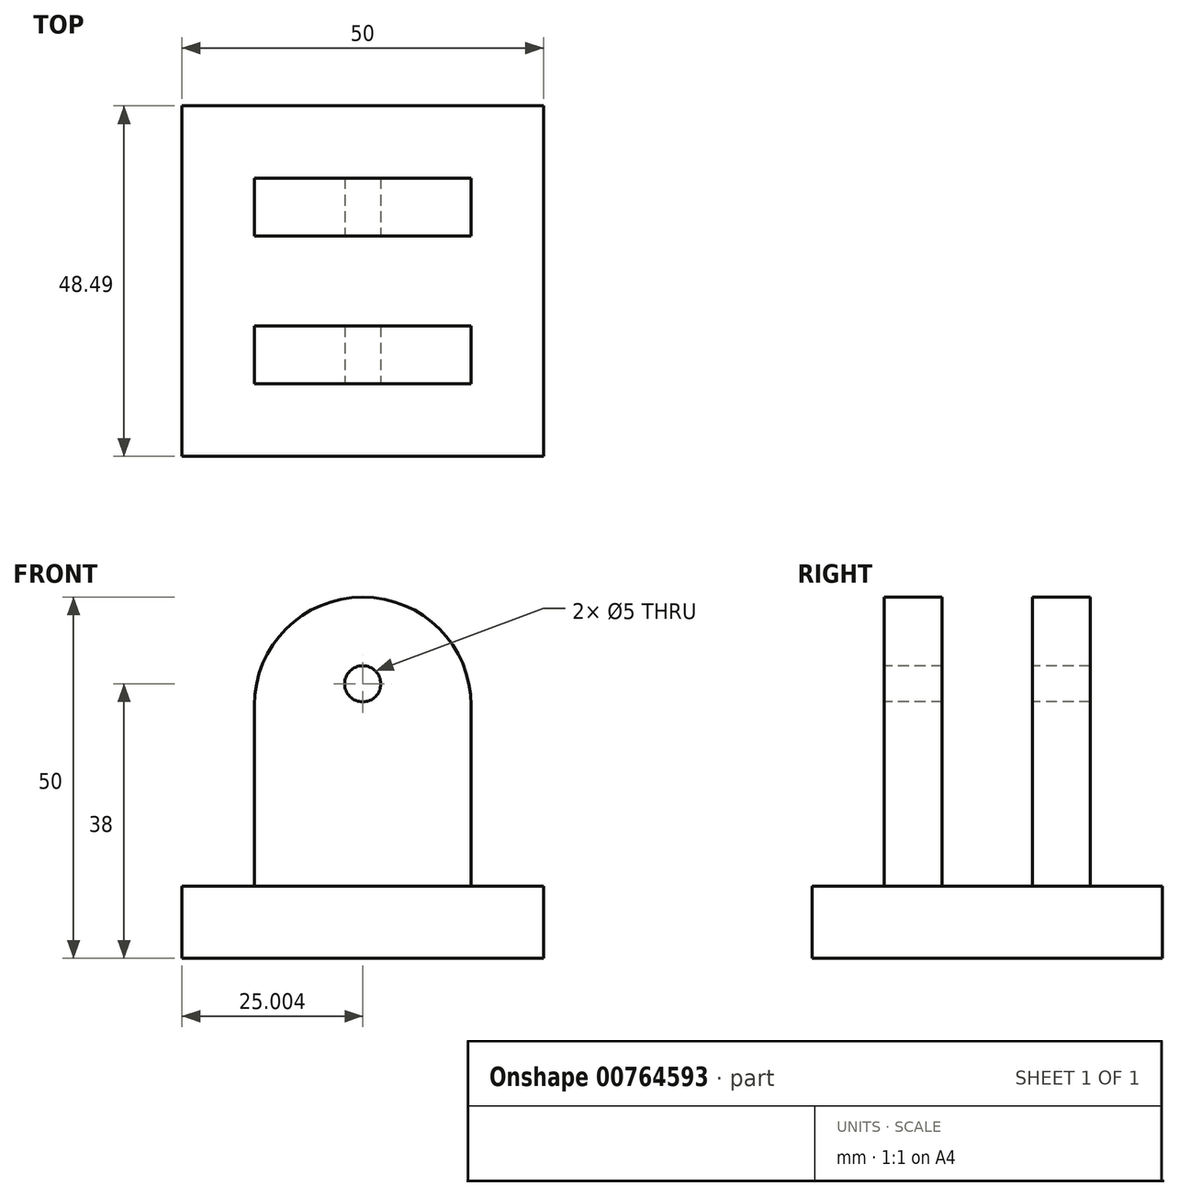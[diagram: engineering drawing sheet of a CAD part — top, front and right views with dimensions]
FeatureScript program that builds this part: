
annotation { "Feature Type Name" : "Feature", "Feature Type Description" : "" }
export const myFeature = defineFeature(function(context is Context, id is Id, definition is map)
    precondition{}
    {
        {
            var Q0;
            Q0=qCreatedBy(makeId("Top.planeOp"),FACE);
            var sketch = newSketch(context, id + "F0", { "sketchPlane" : qUnion([Q0])});
            skLineSegment(sketch, "E0.bottom", {"start": v(-29.26, 25.8) * mm, "end": v(20.74, 25.8) * mm});
            skLineSegment(sketch, "E0.top", {"start": v(-29.26, -22.68) * mm, "end": v(20.74, -22.68) * mm});
            skLineSegment(sketch, "E0.left", {"start": v(-29.26, 25.8) * mm, "end": v(-29.26, -22.68) * mm});
            skLineSegment(sketch, "E0.right", {"start": v(20.74, 25.8) * mm, "end": v(20.74, -22.68) * mm});
            skSolve(sketch);
        }
        {
            var Q0;
            Q0 = qSketchRegion(id + "F0", true);
            extrude(context, id + "F1", {"entities" : qUnion([Q0]), "depth" : 10 * mm, "offsetDistance" : 25 * mm});
        }
        {
            var Q0;
            Q0=makeQuery(id+"F1.opExtrude","CAP_FACE",FACE,{"disambiguationData":[OSD([sQuery(id+"F0.wireOp",EDGE,"E0.bottom"),sQuery(id+"F0.wireOp",EDGE,"E0.top"),sQuery(id+"F0.wireOp",EDGE,"E0.left"),sQuery(id+"F0.wireOp",EDGE,"E0.right")])],"isStart":false});
            var sketch = newSketch(context, id + "F2", { "sketchPlane" : qUnion([Q0])});
            skLineSegment(sketch, "E1.bottom", {"start": v(-19.26, 15.8) * mm, "end": v(10.74, 15.8) * mm});
            skLineSegment(sketch, "E1.top", {"start": v(-19.26, 7.8) * mm, "end": v(10.74, 7.8) * mm});
            skLineSegment(sketch, "E1.left", {"start": v(-19.26, 15.8) * mm, "end": v(-19.26, 7.8) * mm});
            skLineSegment(sketch, "E1.right", {"start": v(10.74, 15.8) * mm, "end": v(10.74, 7.8) * mm});
            skPoint(sketch, "E2.startSnap0", {"position": v(-19.26, 11.8) * mm});
            skSolve(sketch);
        }
        {
            var Q0;
            Q0=makeQuery(id+"F2.imprint","IMPRINT",FACE,{"disambiguationData":[TD([[makeQuery(id+"F2.imprint","IMPRINT",EDGE,{"derivedFrom":sQuery(id+"F2.wireOp",EDGE,"E1.bottom")}),1.0]])]});
            var sketch = newSketch(context, id + "F3", { "sketchPlane" : qUnion([Q0])});
            skLineSegment(sketch, "E3.bottom", {"start": v(-19.26, -4.68) * mm, "end": v(10.74, -4.68) * mm});
            skLineSegment(sketch, "E3.top", {"start": v(-19.26, -12.68) * mm, "end": v(10.74, -12.68) * mm});
            skLineSegment(sketch, "E3.left", {"start": v(-19.26, -4.68) * mm, "end": v(-19.26, -12.68) * mm});
            skLineSegment(sketch, "E3.right", {"start": v(10.74, -4.68) * mm, "end": v(10.74, -12.68) * mm});
            skSolve(sketch);
        }
        {
            var Q0;
            Q0=makeQuery(id+"F2.imprint","IMPRINT",FACE,{"disambiguationData":[TD([[makeQuery(id+"F2.imprint","IMPRINT",EDGE,{"derivedFrom":sQuery(id+"F2.wireOp",EDGE,"E1.bottom")}),-1.0]])]});
            extrude(context, id + "F4", {"entities" : qUnion([Q0]), "operationType" : NewBodyOperationType.ADD, "depth" : 40 * mm, "offsetDistance" : 25 * mm});
        }
        {
            var Q0;
            Q0=makeQuery(id+"F3.imprint","IMPRINT",FACE,{"disambiguationData":[TD([[makeQuery(id+"F3.imprint","IMPRINT",EDGE,{"derivedFrom":sQuery(id+"F3.wireOp",EDGE,"E3.bottom")}),-1.0]])]});
            extrude(context, id + "F5", {"entities" : qUnion([Q0]), "operationType" : NewBodyOperationType.ADD, "depth" : 40 * mm, "offsetDistance" : 25 * mm});
        }
        {
            var Q0;
            Q0=makeQuery(id+"F5.opExtrude","SWEPT_FACE",FACE,{"disambiguationData":[OSD([sQuery(id+"F3.wireOp",EDGE,"E3.top")])]});
            var sketch = newSketch(context, id + "F6", { "sketchPlane" : qUnion([Q0])});
            skCircle(sketch, "E4", {"center": v(-4.26, 38) * mm, "radius": 2.5 * mm});
            skSolve(sketch);
        }
        {
            var Q0;
            Q0=sQuery(id+"F6.wireOp",VERTEX,"E4.center");
            var Q1;
            Q1=makeQuery(id+"F1.opExtrude","SWEPT_BODY",BODY,{"disambiguationData":[OSD([sQuery(id+"F0.wireOp",EDGE,"E0.bottom"),sQuery(id+"F0.wireOp",EDGE,"E0.top"),sQuery(id+"F0.wireOp",EDGE,"E0.left"),sQuery(id+"F0.wireOp",EDGE,"E0.right")])]});
            hole(context, id + "F7", {"style" : HoleStyle.SIMPLE, "endStyle" : HoleEndStyle.THROUGH, "holeDiameter" : 5 * mm, "majorDiameter" : 5 * mm, "isTappedThrough" : true, "tappedDepth" : 12 * mm, "tapClearance" : 3, "locations" : qUnion([Q0]), "scope" : qUnion([Q1])});
        }
        {
            var Q0;
            Q0=makeQuery(id+"F5.opExtrude","CAP_EDGE",EDGE,{"disambiguationData":[OSD([sQuery(id+"F3.wireOp",EDGE,"E3.right")])],"isStart":false});
            var Q1;
            Q1=makeQuery(id+"F5.opExtrude","CAP_EDGE",EDGE,{"disambiguationData":[OSD([sQuery(id+"F3.wireOp",EDGE,"E3.left")])],"isStart":false});
            var Q2;
            Q2=makeQuery(id+"F4.opExtrude","CAP_EDGE",EDGE,{"disambiguationData":[OSD([sQuery(id+"F2.wireOp",EDGE,"E1.right")])],"isStart":false});
            var Q3;
            Q3=makeQuery(id+"F4.opExtrude","CAP_EDGE",EDGE,{"disambiguationData":[OSD([sQuery(id+"F2.wireOp",EDGE,"E1.left")])],"isStart":false});
            fillet(context, id + "F8", {"entities" : qUnion([Q0, Q1, Q2, Q3]), "radius" : 15 * mm, "tangentPropagation" : true, "allowEdgeOverflow" : false});
        }
    });
